# Revit family: Shinhoo_Basic_G
name_source: partatom
category: Оборудование
units: mm (PartAtom-declared; Revit-internal decimal feet)

## family parameters
Всегда вертикально = Нет
Классификация = Нет
На основе рабочей плоскости = Нет
Общий = Нет
При загрузке вырезать с полостями = Нет
Размер круглого соединителя = Использовать диаметр
Тип детали = Вставляется
Точка расчета площади = Нет

## types (4) — shared parameters
ADSK_URL страницы изделия = https://shinhoopump.ru
ADSK_Версия Revit = 2019
ADSK_Версия семейства = 1.0
ADSK_Единица измерения = шт
ADSK_Завод-изготовитель = Shinhoo
ADSK_Количество = 1
ADSK_Коэффициент мощности = 1
ADSK_Материал = Чугун с катафорезным покрытием
ADSK_Напряжение = 230 В
ADSK_Обозначение = ГОСТ 31839-2012, ГОСТ 12.2.007.0-75, ГОСТ 12.2.003-91, ГОСТ Р МЭК 60204-1-2007,  ГОСТ 30804
URL = https://shinhoopump.ru
d1 = 33 мм
d6 = 40 мм
r1 = 17 мм
r1_1 = 18 мм
r1_3 = 25 мм
r6 = 20 мм
Изготовитель = Shinhoo
Класс защиты (IP) = IP44
Разработчик = ООО ПРОРУБИМ
Разработчик (телефон) = +7(495)649-85-43
Скорость вращения = 2850
Степень защиты от удара (IK) = IK04
Тип Насоса = Стандартный циркуляционный насос с «мокрым» ротором
Тип основания = встроенный

## per-type parameters (varying)
| type | ADSK_Код изделия | ADSK_Масса | ADSK_Масса_Текст | ADSK_Наименование | ADSK_Наименование краткое | ADSK_Номинальная мощность | ADSK_Полная мощность | ADSK_Расход жидкости | ADSK_Ток | B | B1 | B2 | DN | H | H1 | H2 | L | b1_20 | Группа модели |
| BASIC 25-12S 180 1x230В - 71211010 | 71211010 | 2.3 | 2.3 | Стандартный циркуляционный насос с «мокрым» ротором BASIC 25-12S 180 1x230В | BASIC 25-12S 180 1x230В | 270 Вт | 270 В·А | 0.001111 м³/с | 1 А | 150 мм | 92 мм | 58 мм | 25 мм | 151 мм | 23 мм | 128 мм | 180 мм | 50 мм | BASIC 25-12S |
| BASIC 25-16 230 1x230В - 71211008 | 71211008 | 12.5 | 12.5 | Стандартный циркуляционный насос с «мокрым» ротором BASIC 25-16 230 1x230В | BASIC 25-16 230 1x230В | 700 Вт | 700 В·А | 0.003056 м³/с | 3 А | 234 мм | 154 мм | 80 мм | 25 мм | 286 мм | 54 мм | 232 мм | 230 мм | 69 мм | BASIC 25-16 |
| BASIC 25-20 230 1x230В - 71211009 | 71211009 | 13.4 | 13.4 | Стандартный циркуляционный насос с «мокрым» ротором BASIC 25-20 230 1x230В | BASIC 25-20 230 1x230В | 1000 Вт | 1000 В·А | 0.003333 м³/с | 5 А | 234 мм | 154 мм | 80 мм | 25 мм | 286 мм | 54 мм | 232 мм | 230 мм | 69 мм | BASIC 25-20 |
| BASIC 32-12 180 1x230В - 71211011 | 71211011 | 8.4 | 8.4 | Стандартный циркуляционный насос с «мокрым» ротором BASIC 32-12 180 1x230В | BASIC 32-12 180 1x230В | 500 Вт | 500 В·А | 0.002778 м³/с | 3 А | 167 мм | 99 мм | 68 мм | 32 мм | 234 мм | 49 мм | 185 мм | 180 мм | 58 мм | BASIC 25-20 |

## geometry (parser evidence)
native form markers: Sweep x2
no freeform markers — native parametric forms only
